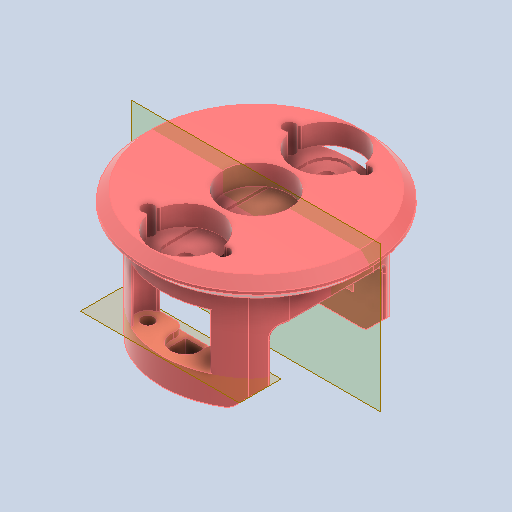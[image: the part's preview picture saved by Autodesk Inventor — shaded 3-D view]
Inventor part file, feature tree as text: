
AUTODESK INVENTOR PART (.ipt)
format: ipt  version: 2022 (Build 260153000, 153)  size: 463,360 bytes
history: native  units: in
note: dims shown in document units (in); Inventor stores cm internally (conversion verified against a paired STEP export)
features: sketch x13, other x3
ambient origin geometry x8: Origin, YZ Plane, XZ Plane, XY Plane, X Axis, Y Axis, Z Axis, Center Point
bodies: Solid1 (feature_tree)
feature tree (16):
  other  "Undercarriage.ipt"
  other  "Solid1::Undercarriage.ipt"
  other  "TaggingFeature1"
  sketch  "Sketch1"  dims[d0=0.3937in]
  sketch  "Sketch2"
  sketch  "Sketch9"
  sketch  "Sketch6"
  sketch  "Sketch7"
  sketch  "Sketch8"
  sketch  "Sketch10"
  sketch  "Sketch11"
  sketch  "Sketch12"
  sketch  "Sketch13"
  sketch  "Sketch14"
  sketch  "Sketch15"
  sketch  "Sketch16"
